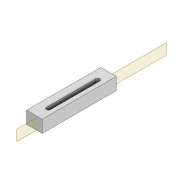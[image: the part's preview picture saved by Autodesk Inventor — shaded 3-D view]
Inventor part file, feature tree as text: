
AUTODESK INVENTOR PART (.ipt)
format: ipt  version: 2022 (Build 260153000, 153)  size: 94,720 bytes
history: native  units: mm
features: extrude x1, plane x1, sketch x1
ambient origin geometry x8: Origin, YZ Plane, XZ Plane, XY Plane, X Axis, Y Axis, Z Axis, Center Point
bodies: Solid1 (feature_tree)
feature tree (3):
  extrude  "Extrusion1"  Depth=40.0mm
  plane  "Work Plane1"
  sketch  "Sketch1"  dims[d0=3.3mm d1=40.0mm d2=10.0mm d3=10.0mm d4=10.0mm d5=10.0mm d6=6.0mm d7=10.0mm d8=0.0mm]
